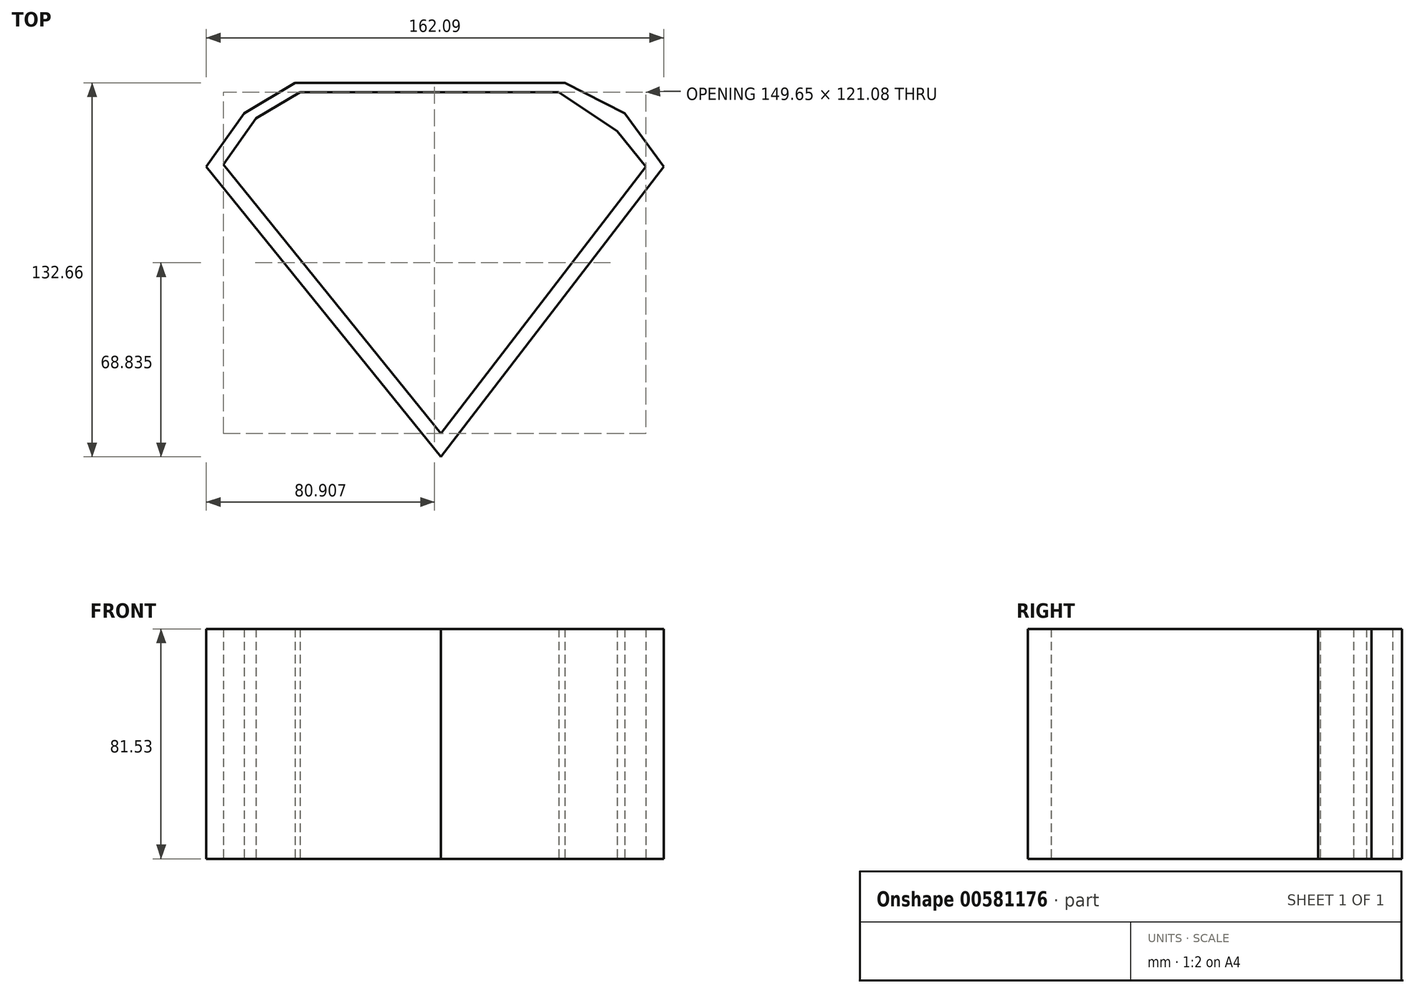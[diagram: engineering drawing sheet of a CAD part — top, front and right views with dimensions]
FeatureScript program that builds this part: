
annotation { "Feature Type Name" : "Feature", "Feature Type Description" : "" }
export const myFeature = defineFeature(function(context is Context, id is Id, definition is map)
    precondition{}
    {
        {
            var Q0;
            Q0=qCreatedBy(makeId("Top.planeOp"),FACE);
            var sketch = newSketch(context, id + "F0", { "sketchPlane" : qUnion([Q0])});
            skLineSegment(sketch, "E0", {"start": v(-230.17, 39.69) * mm, "end": v(-134.47, 39.69) * mm});
            skLineSegment(sketch, "E1", {"start": v(-134.47, 39.69) * mm, "end": v(-113.32, 28.9) * mm});
            skLineSegment(sketch, "E2", {"start": v(-113.32, 28.9) * mm, "end": v(-99.47, 9.98) * mm});
            skLineSegment(sketch, "E3", {"start": v(-230.17, 39.69) * mm, "end": v(-248.2, 28.9) * mm});
            skLineSegment(sketch, "E4", {"start": v(-248.2, 28.9) * mm, "end": v(-261.56, 9.98) * mm});
            skLineSegment(sketch, "E5", {"start": v(-261.56, 9.98) * mm, "end": v(-178.41, -92.97) * mm});
            skLineSegment(sketch, "E6", {"start": v(-178.41, -92.97) * mm, "end": v(-99.47, 9.98) * mm});
            skLineSegment(sketch, "E7", {"start": v(-243.97, 27.06) * mm, "end": v(-228.33, 36.4) * mm});
            skLineSegment(sketch, "E8", {"start": v(-243.97, 27.06) * mm, "end": v(-255.48, 10.75) * mm});
            skLineSegment(sketch, "E9", {"start": v(-255.48, 10.75) * mm, "end": v(-178.41, -84.67) * mm});
            skLineSegment(sketch, "E10", {"start": v(-178.41, -84.67) * mm, "end": v(-105.83, 9.98) * mm});
            skLineSegment(sketch, "E11", {"start": v(-105.83, 9.98) * mm, "end": v(-115.93, 22.48) * mm});
            skLineSegment(sketch, "E12", {"start": v(-228.33, 36.4) * mm, "end": v(-136.63, 36.4) * mm});
            skLineSegment(sketch, "E13", {"start": v(-136.63, 36.4) * mm, "end": v(-115.93, 22.48) * mm});
            skSolve(sketch);
        }
        {
            var Q0;
            Q0=makeQuery(id+"F0.imprint","IMPRINT",FACE,{"disambiguationData":[TD([[makeQuery(id+"F0.imprint","IMPRINT",EDGE,{"derivedFrom":sQuery(id+"F0.wireOp",EDGE,"E0")}),-1.0]])]});
            extrude(context, id + "F1", {"entities" : qUnion([Q0]), "depth" : 81.53 * mm, "offsetDistance" : 25.4 * mm});
        }
    });
